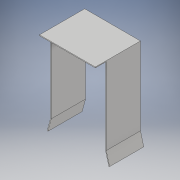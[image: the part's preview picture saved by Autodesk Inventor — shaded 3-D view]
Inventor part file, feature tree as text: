
AUTODESK INVENTOR PART (.ipt)
format: ipt  version: 2019 (Build 230136000, 136)  size: 133,120 bytes
history: native  units: in
note: dims shown in document units (in); Inventor stores cm internally (conversion verified against a paired STEP export)
features: extrude x2, plane x1
ambient origin geometry x8: Origin, YZ Plane, XZ Plane, XY Plane, X Axis, Y Axis, Z Axis, Center Point
bodies: Body1 (feature_tree)
feature tree (3):
  extrude  "Extrusion4"  Depth=0.0625in
  extrude  "Extrusion5"  Depth=0.0625in
  plane  "Work Plane3"
